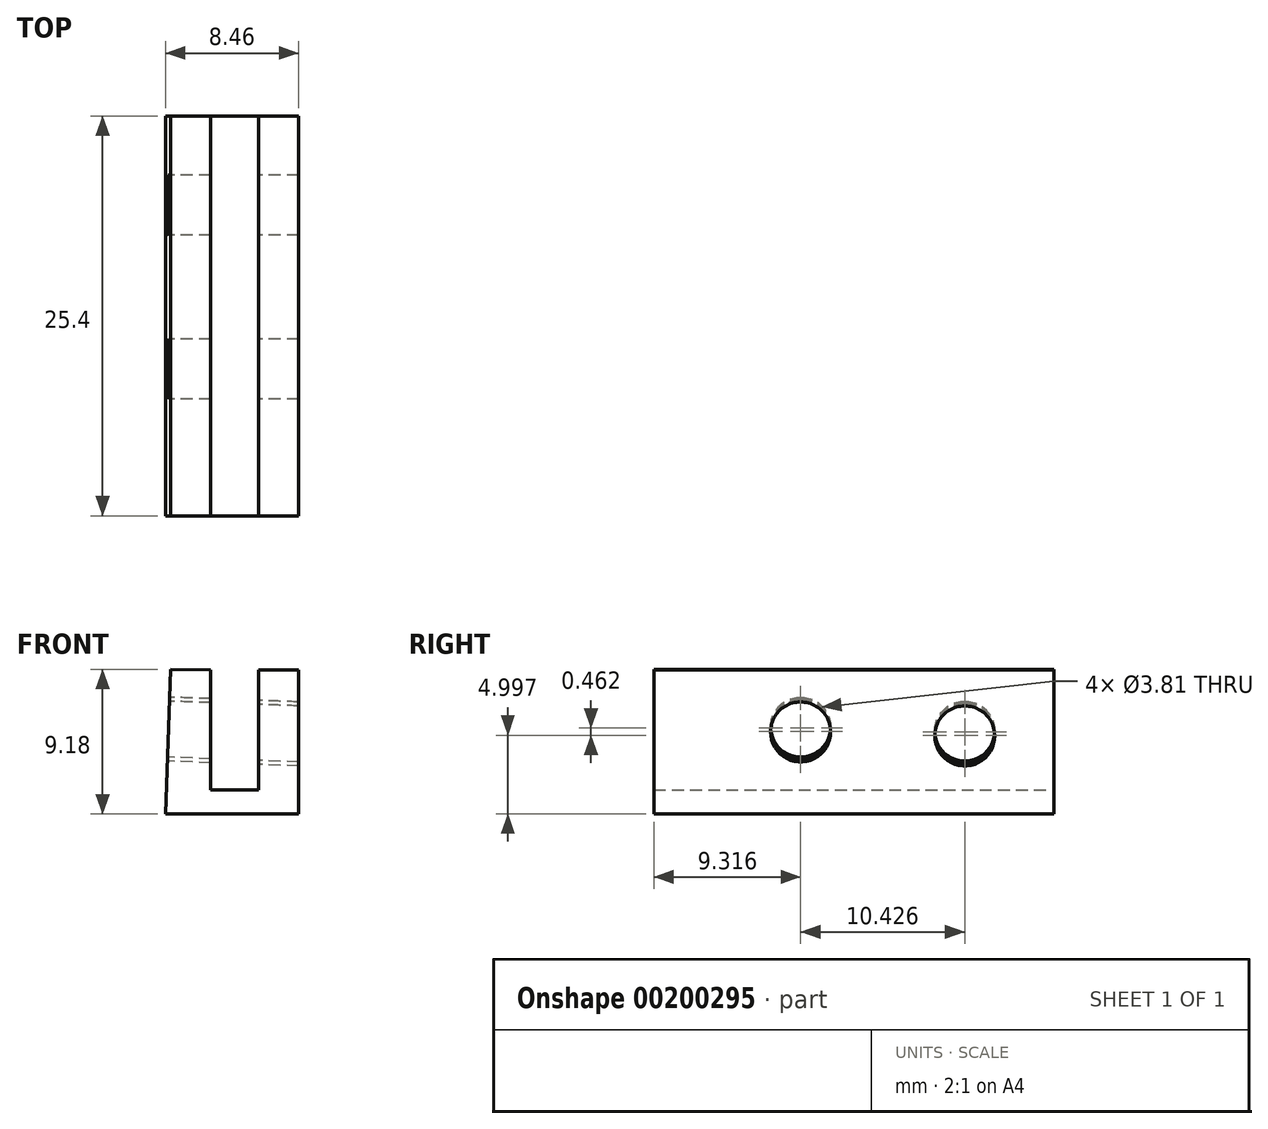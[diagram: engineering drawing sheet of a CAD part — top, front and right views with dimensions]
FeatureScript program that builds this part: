
annotation { "Feature Type Name" : "Feature", "Feature Type Description" : "" }
export const myFeature = defineFeature(function(context is Context, id is Id, definition is map)
    precondition{}
    {
        {
            var Q0;
            Q0=qCreatedBy(makeId("Front.planeOp"),FACE);
            var sketch = newSketch(context, id + "F0", { "sketchPlane" : qUnion([Q0])});
            skLineSegment(sketch, "E0", {"start": v(2.35, 3.6) * mm, "end": v(2.02, -5.59) * mm});
            skLineSegment(sketch, "E1", {"start": v(2.02, -5.59) * mm, "end": v(10.48, -5.59) * mm});
            skLineSegment(sketch, "E2", {"start": v(10.48, -5.59) * mm, "end": v(10.48, 3.55) * mm});
            skLineSegment(sketch, "E3", {"start": v(10.48, 3.55) * mm, "end": v(7.94, 3.55) * mm});
            skLineSegment(sketch, "E4", {"start": v(7.94, 3.55) * mm, "end": v(7.94, -4.07) * mm});
            skLineSegment(sketch, "E5", {"start": v(7.94, -4.07) * mm, "end": v(4.9, -4.07) * mm});
            skLineSegment(sketch, "E6", {"start": v(4.9, -4.07) * mm, "end": v(4.9, 3.55) * mm});
            skLineSegment(sketch, "E7", {"start": v(4.9, 3.55) * mm, "end": v(2.35, 3.6) * mm});
            skSolve(sketch);
        }
        {
            var Q0;
            Q0=makeQuery(id+"F0.imprint","IMPRINT",FACE,{"disambiguationData":[TD([[makeQuery(id+"F0.imprint","IMPRINT",EDGE,{"derivedFrom":sQuery(id+"F0.wireOp",EDGE,"E0")}),1.0]])]});
            extrude(context, id + "F1", {"entities" : qUnion([Q0]), "depth" : 25.4 * mm});
        }
        {
            var Q0;
            Q0=makeQuery(id+"F1.opExtrude","SWEPT_FACE",FACE,{"disambiguationData":[OSD([sQuery(id+"F0.wireOp",EDGE,"E0")])]});
            var sketch = newSketch(context, id + "F2", { "sketchPlane" : qUnion([Q0])});
            skCircle(sketch, "E8", {"center": v(5.66, -0.25) * mm, "radius": 1.9 * mm});
            skCircle(sketch, "E9", {"center": v(16.08, 0) * mm, "radius": 1.9 * mm});
            skSolve(sketch);
        }
        {
            var Q0;
            Q0 = qSketchRegion(id + "F2", true);
            extrude(context, id + "F3", {"entities" : qUnion([Q0]), "operationType" : NewBodyOperationType.REMOVE, "oppositeDirection" : true, "depth" : 25.4 * mm});
        }
    });
